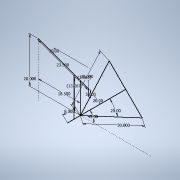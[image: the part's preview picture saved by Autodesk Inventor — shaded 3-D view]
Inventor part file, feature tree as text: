
AUTODESK INVENTOR PART (.ipt)
format: ipt  version: 2022.2 (Build 262287000, 287)  size: 103,936 bytes
history: native  units: in
note: dims shown in document units (in); Inventor stores cm internally (conversion verified against a paired STEP export)
features: sketch x1
ambient origin geometry x8: Origin, YZ Plane, XZ Plane, XY Plane, X Axis, Y Axis, Z Axis, Center Point
feature tree (1):
  sketch  "Sketch1"  dims[d1=23.5in d2=0.1374in d3=3.0in d5=18.5in d6=20.0in d8=45.0deg d9=30.0in d10=0.1374in d11=30.0in d12=0.1374in d13=13.2666in d14=3.5828in d15=8.0in]
